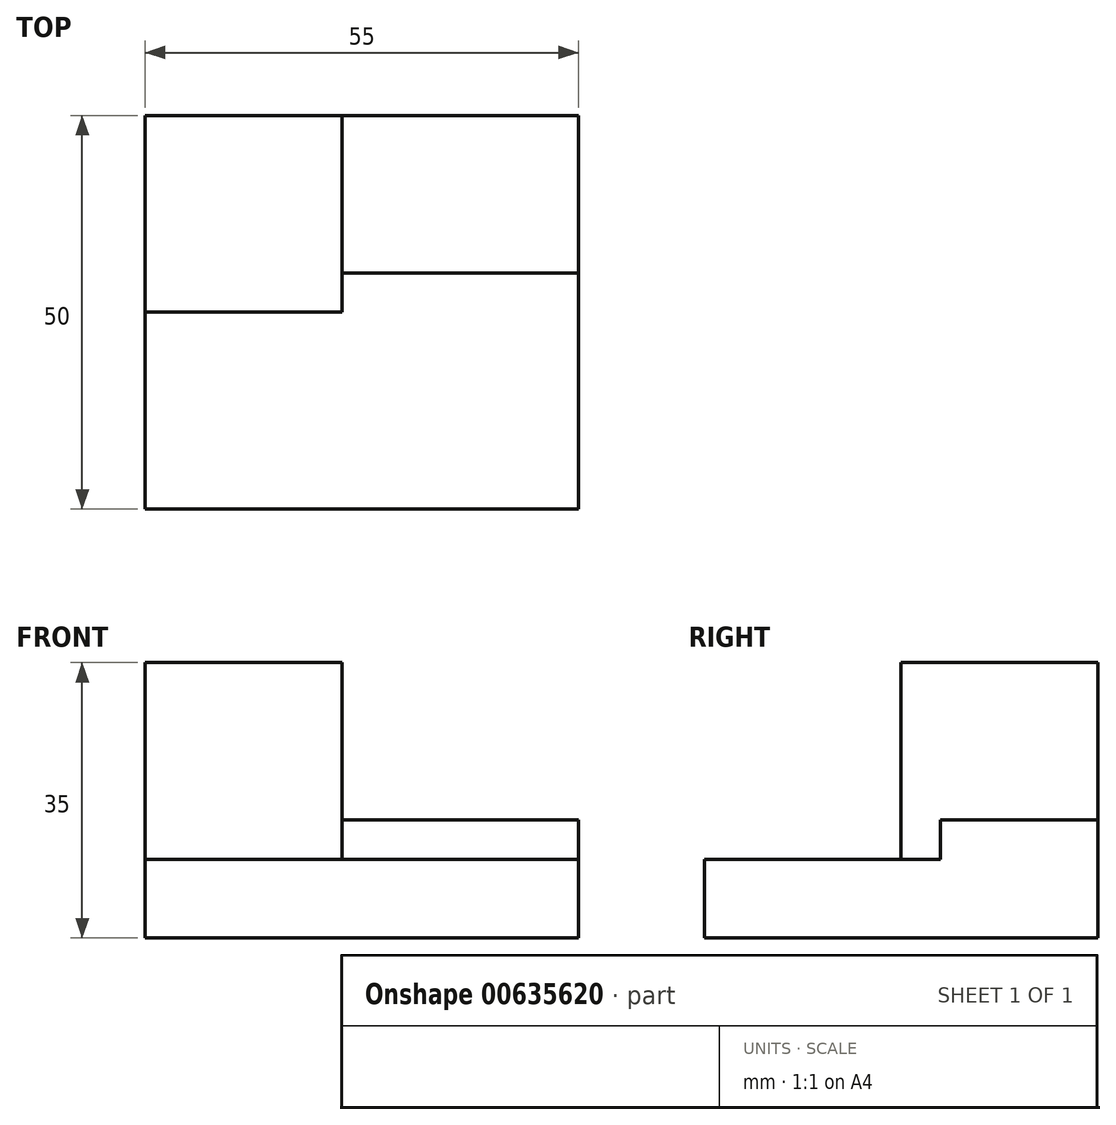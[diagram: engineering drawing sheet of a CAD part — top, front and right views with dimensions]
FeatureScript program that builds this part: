
annotation { "Feature Type Name" : "Feature", "Feature Type Description" : "" }
export const myFeature = defineFeature(function(context is Context, id is Id, definition is map)
    precondition{}
    {
        {
            var Q0;
            Q0=qCreatedBy(makeId("Top.planeOp"),FACE);
            var sketch = newSketch(context, id + "F0", { "sketchPlane" : qUnion([Q0])});
            skLineSegment(sketch, "E0.bottom", {"start": v(27.5, -25) * mm, "end": v(-27.5, -25) * mm});
            skLineSegment(sketch, "E0.top", {"start": v(27.5, 25) * mm, "end": v(-27.5, 25) * mm});
            skLineSegment(sketch, "E0.left", {"start": v(27.5, -25) * mm, "end": v(27.5, 25) * mm});
            skLineSegment(sketch, "E0.right", {"start": v(-27.5, -25) * mm, "end": v(-27.5, 25) * mm});
            skPoint(sketch, "E0.middle", {"position": v(0, 0) * mm});
            skSolve(sketch);
        }
        {
            var Q0;
            Q0=makeQuery(id+"F0.imprint","IMPRINT",FACE,{"disambiguationData":[TD([[makeQuery(id+"F0.imprint","IMPRINT",EDGE,{"derivedFrom":sQuery(id+"F0.wireOp",EDGE,"E0.bottom")}),-1.0]])]});
            extrude(context, id + "F1", {"entities" : qUnion([Q0]), "depth" : 10 * mm, "offsetDistance" : 25 * mm});
        }
        {
            var Q0;
            Q0=makeQuery(id+"F1.opExtrude","CAP_FACE",FACE,{"disambiguationData":[OSD([sQuery(id+"F0.wireOp",EDGE,"E0.bottom"),sQuery(id+"F0.wireOp",EDGE,"E0.top"),sQuery(id+"F0.wireOp",EDGE,"E0.left"),sQuery(id+"F0.wireOp",EDGE,"E0.right")])],"isStart":false});
            var sketch = newSketch(context, id + "F2", { "sketchPlane" : qUnion([Q0])});
            skLineSegment(sketch, "E1", {"start": v(-27.5, 0) * mm, "end": v(-2.5, 0) * mm});
            skLineSegment(sketch, "E2", {"start": v(-2.5, 0) * mm, "end": v(-2.5, 25) * mm});
            skLineSegment(sketch, "E3", {"start": v(-2.5, 25) * mm, "end": v(-27.5, 25) * mm});
            skLineSegment(sketch, "E4", {"start": v(-27.5, 25) * mm, "end": v(-27.5, 0) * mm});
            skSolve(sketch);
        }
        {
            var Q0;
            Q0 = qSketchRegion(id + "F2", true);
            extrude(context, id + "F3", {"entities" : qUnion([Q0]), "operationType" : NewBodyOperationType.ADD, "depth" : 25 * mm, "offsetDistance" : 25 * mm});
        }
        {
            var Q0;
            Q0=makeQuery(id+"F1.opExtrude","CAP_FACE",FACE,{"disambiguationData":[OSD([sQuery(id+"F0.wireOp",EDGE,"E0.bottom"),sQuery(id+"F0.wireOp",EDGE,"E0.top"),sQuery(id+"F0.wireOp",EDGE,"E0.left"),sQuery(id+"F0.wireOp",EDGE,"E0.right")])],"isStart":false});
            var sketch = newSketch(context, id + "F4", { "sketchPlane" : qUnion([Q0])});
            skLineSegment(sketch, "E5", {"start": v(0, 0) * mm, "end": v(0, 5) * mm, "construction": true});
            skLineSegment(sketch, "E6", {"start": v(0, 5) * mm, "end": v(-2.5, 5) * mm});
            skLineSegment(sketch, "E7", {"start": v(-2.5, 5) * mm, "end": v(27.5, 5) * mm});
            skLineSegment(sketch, "E8", {"start": v(27.5, 5) * mm, "end": v(27.5, 25) * mm});
            skLineSegment(sketch, "E9", {"start": v(27.5, 25) * mm, "end": v(-2.5, 25) * mm});
            skLineSegment(sketch, "E10", {"start": v(-2.5, 25) * mm, "end": v(-2.5, 5) * mm});
            skSolve(sketch);
        }
        {
            var Q0;
            Q0 = qSketchRegion(id + "F4", true);
            extrude(context, id + "F5", {"entities" : qUnion([Q0]), "operationType" : NewBodyOperationType.ADD, "depth" : 5 * mm, "offsetDistance" : 25 * mm});
        }
    });
